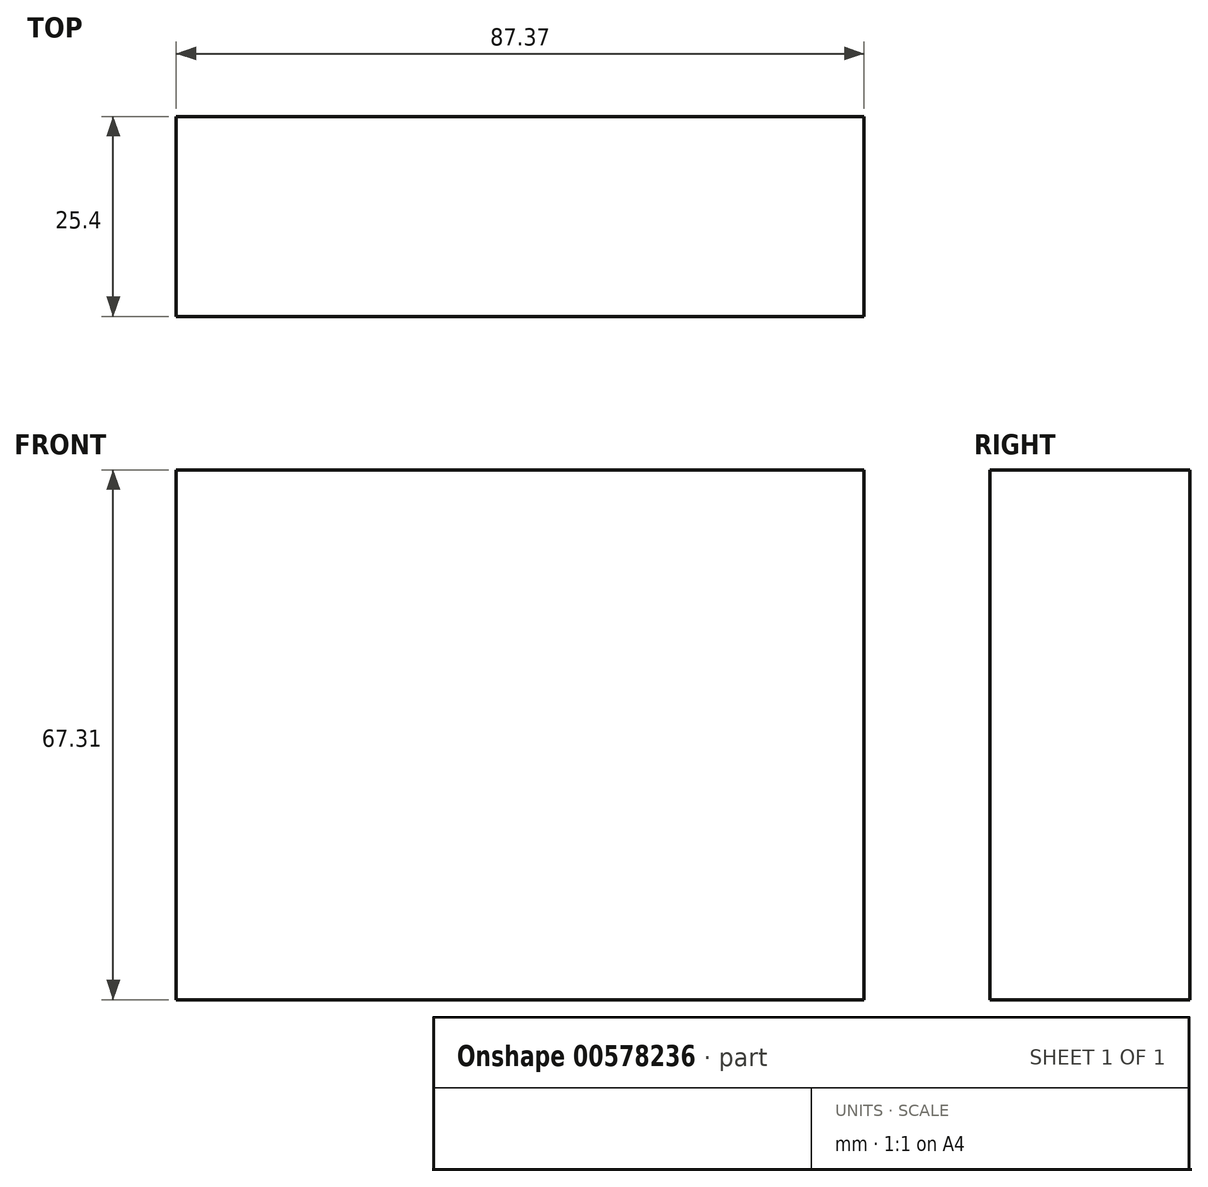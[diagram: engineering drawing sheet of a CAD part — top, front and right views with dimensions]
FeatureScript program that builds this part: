
annotation { "Feature Type Name" : "Feature", "Feature Type Description" : "" }
export const myFeature = defineFeature(function(context is Context, id is Id, definition is map)
    precondition{}
    {
        {
            var Q0;
            Q0=qCreatedBy(makeId("Front.planeOp"),FACE);
            var sketch = newSketch(context, id + "F0", { "sketchPlane" : qUnion([Q0])});
            skLineSegment(sketch, "E0.bottom", {"start": v(0, 0) * mm, "end": v(87.37, 0) * mm});
            skLineSegment(sketch, "E0.top", {"start": v(0, 67.31) * mm, "end": v(87.37, 67.31) * mm});
            skLineSegment(sketch, "E0.left", {"start": v(0, 0) * mm, "end": v(0, 67.31) * mm});
            skLineSegment(sketch, "E0.right", {"start": v(87.37, 0) * mm, "end": v(87.37, 67.31) * mm});
            skSolve(sketch);
        }
        {
            var Q0;
            Q0 = qSketchRegion(id + "F0", true);
            extrude(context, id + "F1", {"entities" : qUnion([Q0]), "depth" : 25.4 * mm, "offsetDistance" : 25.4 * mm});
        }
    });
